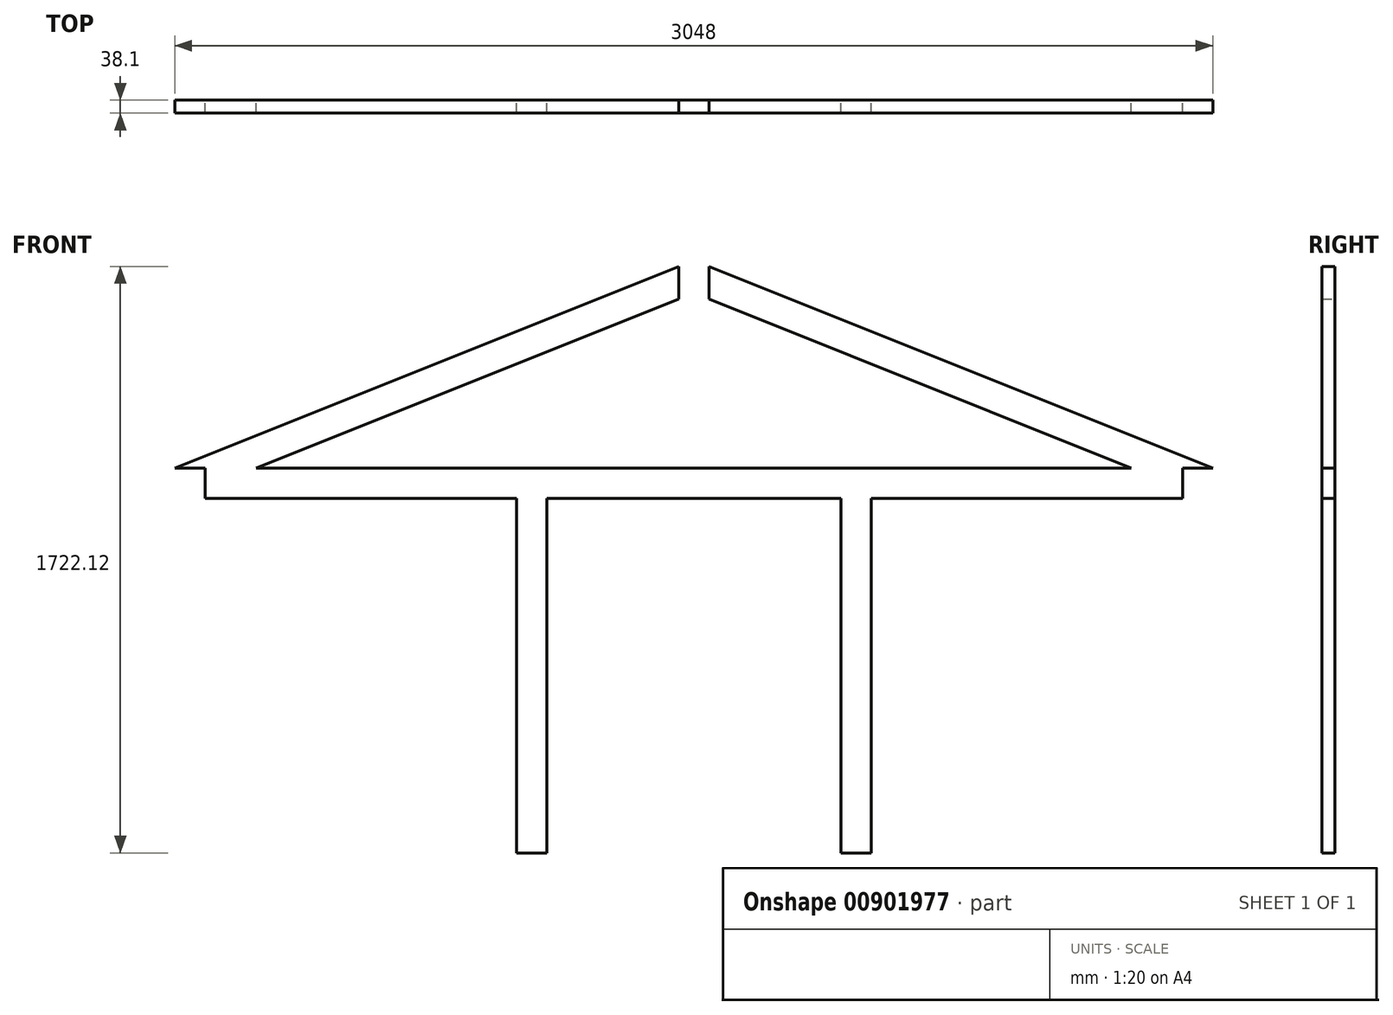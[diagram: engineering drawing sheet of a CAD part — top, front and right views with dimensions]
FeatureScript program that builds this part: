
annotation { "Feature Type Name" : "Feature", "Feature Type Description" : "" }
export const myFeature = defineFeature(function(context is Context, id is Id, definition is map)
    precondition{}
    {
        {
            var Q0;
            Q0=qCreatedBy(makeId("Front.planeOp"),FACE);
            var sketch = newSketch(context, id + "F0", { "sketchPlane" : qUnion([Q0])});
            skLineSegment(sketch, "E0.bottom", {"start": v(-1524, 914.4) * mm, "end": v(1524, 914.4) * mm});
            skLineSegment(sketch, "E0.top", {"start": v(-1524, -914.4) * mm, "end": v(1524, -914.4) * mm});
            skLineSegment(sketch, "E0.left", {"start": v(-1524, 914.4) * mm, "end": v(-1524, -914.4) * mm});
            skLineSegment(sketch, "E0.right", {"start": v(1524, 914.4) * mm, "end": v(1524, -914.4) * mm});
            skPoint(sketch, "E0.middle", {"position": v(0, 0) * mm});
            skLineSegment(sketch, "E1", {"start": v(-1524, -914.4) * mm, "end": v(-1524, 304.8) * mm});
            skLineSegment(sketch, "E2", {"start": v(1524, -914.4) * mm, "end": v(1524, 304.8) * mm});
            skLineSegment(sketch, "E3", {"start": v(-1524, 304.8) * mm, "end": v(0, 914.4) * mm});
            skLineSegment(sketch, "E4", {"start": v(1524, 304.8) * mm, "end": v(0, 914.4) * mm});
            skLineSegment(sketch, "E5", {"start": v(-1524, 304.8) * mm, "end": v(-1435.1, 304.8) * mm});
            skLineSegment(sketch, "E6", {"start": v(-1435.1, 304.8) * mm, "end": v(-1435.1, -914.4) * mm});
            skLineSegment(sketch, "E7", {"start": v(1524, 304.8) * mm, "end": v(1435.1, 304.8) * mm});
            skLineSegment(sketch, "E8", {"start": v(1435.1, 304.8) * mm, "end": v(1435.1, -914.4) * mm});
            skLineSegment(sketch, "E9.bottom", {"start": v(-1435.1, 304.8) * mm, "end": v(1435.1, 304.8) * mm});
            skLineSegment(sketch, "E9.top", {"start": v(-1435.1, 215.9) * mm, "end": v(1435.1, 215.9) * mm});
            skLineSegment(sketch, "E9.left", {"start": v(-1435.1, 304.8) * mm, "end": v(-1435.1, 215.9) * mm});
            skLineSegment(sketch, "E9.right", {"start": v(1435.1, 304.8) * mm, "end": v(1435.1, 215.9) * mm});
            skLineSegment(sketch, "E10", {"start": v(-762, 609.6) * mm, "end": v(-728.98, 527.06) * mm});
            skLineSegment(sketch, "E11", {"start": v(762, 609.6) * mm, "end": v(728.98, 527.06) * mm});
            skLineSegment(sketch, "E12", {"start": v(-728.98, 527.06) * mm, "end": v(-1284.63, 304.8) * mm});
            skLineSegment(sketch, "E13", {"start": v(728.98, 527.06) * mm, "end": v(1284.63, 304.8) * mm});
            skLineSegment(sketch, "E14", {"start": v(0, 304.8) * mm, "end": v(-44.45, 304.8) * mm});
            skLineSegment(sketch, "E15", {"start": v(-44.45, 304.8) * mm, "end": v(-44.45, 896.62) * mm});
            skLineSegment(sketch, "E16", {"start": v(0, 304.8) * mm, "end": v(44.45, 304.8) * mm});
            skLineSegment(sketch, "E17", {"start": v(44.45, 304.8) * mm, "end": v(44.45, 896.62) * mm});
            skLineSegment(sketch, "E18", {"start": v(-728.98, 527.06) * mm, "end": v(-44.45, 800.87) * mm});
            skLineSegment(sketch, "E19", {"start": v(728.98, 527.06) * mm, "end": v(44.45, 800.87) * mm});
            skLineSegment(sketch, "E20.bottom", {"start": v(-1435.1, -914.4) * mm, "end": v(1435.1, -914.4) * mm});
            skLineSegment(sketch, "E20.top", {"start": v(-1435.1, -825.5) * mm, "end": v(1435.1, -825.5) * mm});
            skLineSegment(sketch, "E20.left", {"start": v(-1435.1, -914.4) * mm, "end": v(-1435.1, -825.5) * mm});
            skLineSegment(sketch, "E20.right", {"start": v(1435.1, -914.4) * mm, "end": v(1435.1, -825.5) * mm});
            skLineSegment(sketch, "E21", {"start": v(-1435.1, -825.5) * mm, "end": v(-520.7, -825.5) * mm});
            skLineSegment(sketch, "E22", {"start": v(-520.7, -825.5) * mm, "end": v(-520.7, 215.9) * mm});
            skLineSegment(sketch, "E23", {"start": v(-520.7, 215.9) * mm, "end": v(-431.8, 215.9) * mm});
            skLineSegment(sketch, "E24", {"start": v(-431.8, 215.9) * mm, "end": v(-431.8, -825.5) * mm});
            skLineSegment(sketch, "E25", {"start": v(1435.1, -825.5) * mm, "end": v(520.7, -825.5) * mm});
            skLineSegment(sketch, "E26", {"start": v(520.7, -825.5) * mm, "end": v(520.7, 215.9) * mm});
            skLineSegment(sketch, "E27", {"start": v(520.7, 215.9) * mm, "end": v(431.8, 215.9) * mm});
            skLineSegment(sketch, "E28", {"start": v(431.8, 215.9) * mm, "end": v(431.8, -825.5) * mm});
            skSolve(sketch);
        }
        {
            var Q0;
            {var subQ0=sQuery(id+"F0.wireOp",EDGE,"E10");Q0=makeQuery(id+"F0.imprint","IMPRINT",FACE,{"disambiguationData":[TD([[makeQuery(id+"F0.imprint","IMPRINT",EDGE,{"derivedFrom":subQ0}),1.0]])]});}
            var Q1;
            {var subQ1=sQuery(id+"F0.wireOp",EDGE,"E5");Q1=makeQuery(id+"F0.imprint","IMPRINT",FACE,{"disambiguationData":[TD([[makeQuery(id+"F0.imprint","IMPRINT",EDGE,{"derivedFrom":subQ1}),1.0]])]});}
            var Q2;
            {var subQ0=sQuery(id+"F0.wireOp",EDGE,"E14");Q2=makeQuery(id+"F0.imprint","IMPRINT",FACE,{"disambiguationData":[TD([[makeQuery(id+"F0.imprint","IMPRINT",EDGE,{"derivedFrom":subQ0}),-1.0]])]});}
            var Q3;
            {var subQ2=sQuery(id+"F0.wireOp",EDGE,"E7");Q3=makeQuery(id+"F0.imprint","IMPRINT",FACE,{"disambiguationData":[TD([[makeQuery(id+"F0.imprint","IMPRINT",EDGE,{"derivedFrom":subQ2}),-1.0]])]});}
            var Q4;
            Q4=makeQuery(id+"F0.imprint","IMPRINT",FACE,{"disambiguationData":[TD([[makeQuery(id+"F0.imprint","IMPRINT",EDGE,{"derivedFrom":sQuery(id+"F0.wireOp",EDGE,"E9.top")}),1.0]])]});
            var Q5;
            {var subQ0=sQuery(id+"F0.wireOp",EDGE,"E11");Q5=makeQuery(id+"F0.imprint","IMPRINT",FACE,{"disambiguationData":[TD([[makeQuery(id+"F0.imprint","IMPRINT",EDGE,{"derivedFrom":subQ0}),-1.0]])]});}
            var Q6;
            {var subQ0=sQuery(id+"F0.wireOp",EDGE,"E2");Q6=makeQuery(id+"F0.imprint","IMPRINT",FACE,{"disambiguationData":[TD([[makeQuery(id+"F0.imprint","IMPRINT",EDGE,{"derivedFrom":subQ0}),1.0]])]});}
            var Q7;
            Q7=makeQuery(id+"F0.imprint","IMPRINT",FACE,{"disambiguationData":[TD([[makeQuery(id+"F0.imprint","IMPRINT",EDGE,{"derivedFrom":sQuery(id+"F0.wireOp",EDGE,"E20.bottom")}),1.0]])]});
            var Q8;
            {var subQ0=sQuery(id+"F0.wireOp",EDGE,"E1");Q8=makeQuery(id+"F0.imprint","IMPRINT",FACE,{"disambiguationData":[TD([[makeQuery(id+"F0.imprint","IMPRINT",EDGE,{"derivedFrom":subQ0}),-1.0]])]});}
            var Q9;
            {var subQ0=sQuery(id+"F0.wireOp",EDGE,"E22");Q9=makeQuery(id+"F0.imprint","IMPRINT",FACE,{"disambiguationData":[TD([[makeQuery(id+"F0.imprint","IMPRINT",EDGE,{"derivedFrom":subQ0}),-1.0]])]});}
            var Q10;
            {var subQ0=sQuery(id+"F0.wireOp",EDGE,"E26");Q10=makeQuery(id+"F0.imprint","IMPRINT",FACE,{"disambiguationData":[TD([[makeQuery(id+"F0.imprint","IMPRINT",EDGE,{"derivedFrom":subQ0}),1.0]])]});}
            extrude(context, id + "F1", {"entities" : qUnion([Q0, Q1, Q2, Q3, Q4, Q5, Q6, Q7, Q8, Q9, Q10]), "depth" : 38.1 * mm, "offsetDistance" : 25.4 * mm});
        }
    });
